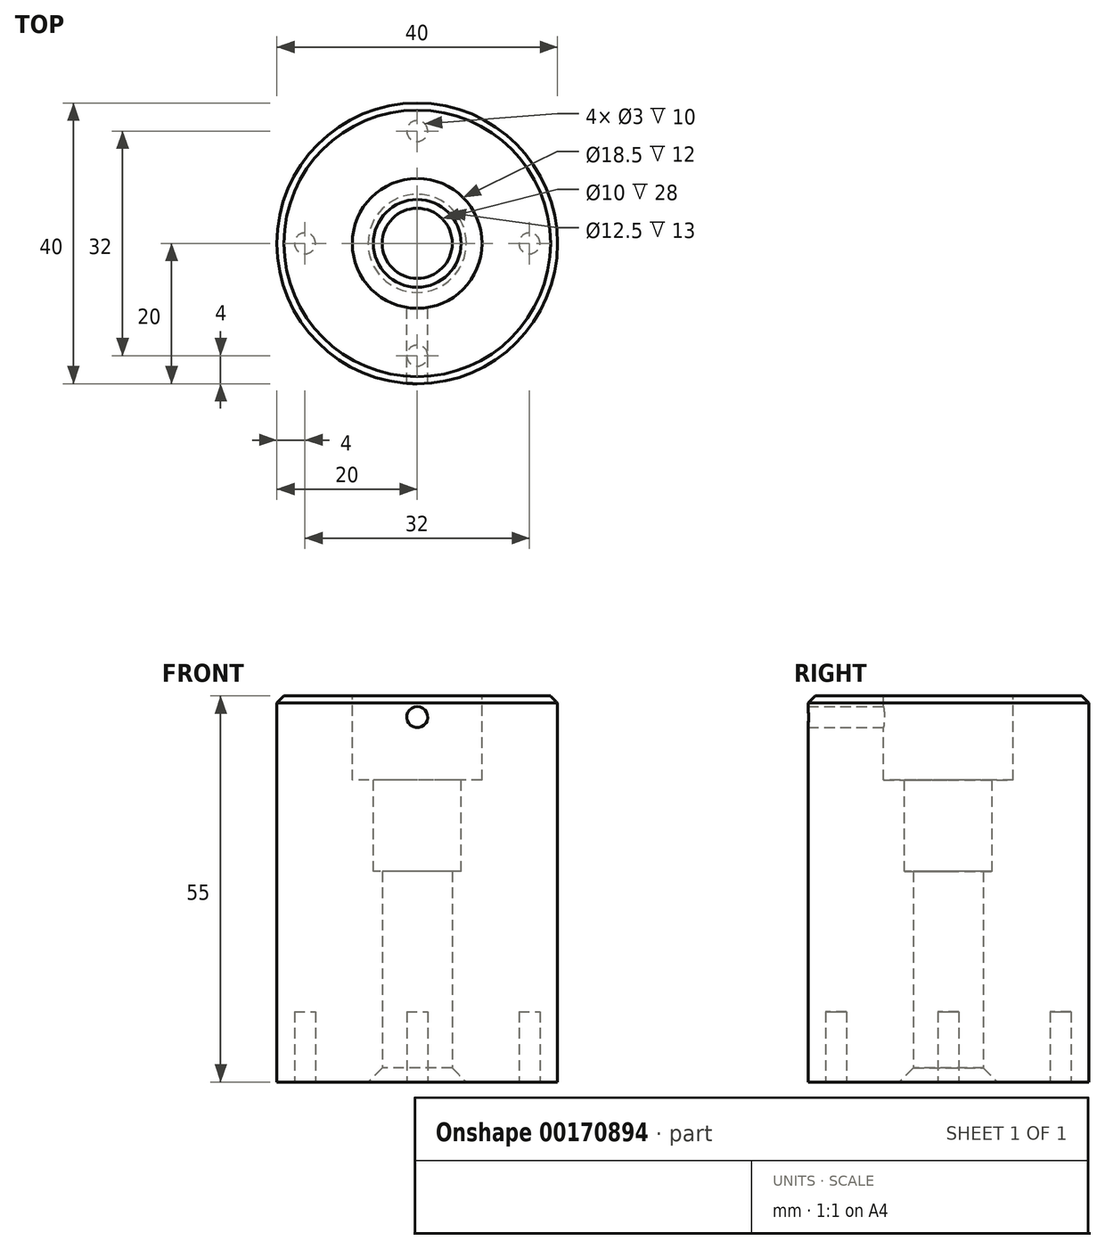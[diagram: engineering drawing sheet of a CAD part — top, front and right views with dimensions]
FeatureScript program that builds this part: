
annotation { "Feature Type Name" : "Feature", "Feature Type Description" : "" }
export const myFeature = defineFeature(function(context is Context, id is Id, definition is map)
    precondition{}
    {
        {
            var Q0;
            Q0=qCreatedBy(makeId("Top.planeOp"),FACE);
            var sketch = newSketch(context, id + "F0", { "sketchPlane" : qUnion([Q0])});
            skCircle(sketch, "E0", {"center": v(0, 0) * mm, "radius": 20 * mm});
            skCircle(sketch, "E1", {"center": v(0, 0) * mm, "radius": 5 * mm});
            skSolve(sketch);
        }
        {
            var Q0;
            Q0 = qSketchRegion(id + "F0", true);
            extrude(context, id + "F1", {"entities" : qUnion([Q0]), "depth" : 55 * mm});
        }
        {
            var Q0;
            Q0=makeQuery(id+"F1.opExtrude","CAP_FACE",FACE,{"disambiguationData":[OSD([sQuery(id+"F0.wireOp",EDGE,"E0"),sQuery(id+"F0.wireOp",EDGE,"E1")])],"isStart":false});
            var sketch = newSketch(context, id + "F2", { "sketchPlane" : qUnion([Q0])});
            skCircle(sketch, "E2", {"center": v(0, 0) * mm, "radius": 9.25 * mm});
            skSolve(sketch);
        }
        {
            var Q0;
            Q0 = qSketchRegion(id + "F2", true);
            extrude(context, id + "F3", {"entities" : qUnion([Q0]), "operationType" : NewBodyOperationType.REMOVE, "oppositeDirection" : true, "depth" : 12 * mm});
        }
        {
            var Q0;
            Q0=makeQuery(id+"F3.boolean.opBoolean","COPY",FACE,{"derivedFrom":makeQuery(id+"F3.opExtrude","CAP_FACE",FACE,{"disambiguationData":[OSD([sQuery(id+"F2.wireOp",EDGE,"E2")])],"isStart":false})});
            var sketch = newSketch(context, id + "F4", { "sketchPlane" : qUnion([Q0])});
            skCircle(sketch, "E3", {"center": v(0, 0) * mm, "radius": 6.25 * mm});
            skSolve(sketch);
        }
        {
            var Q0;
            Q0 = qSketchRegion(id + "F4", true);
            extrude(context, id + "F5", {"entities" : qUnion([Q0]), "operationType" : NewBodyOperationType.REMOVE, "oppositeDirection" : true, "depth" : 13 * mm});
        }
        {
            var Q0;
            Q0=makeQuery(id+"F3.boolean.opBoolean","COPY",EDGE,{"derivedFrom":makeQuery(id+"F3.opExtrude","CAP_EDGE",EDGE,{"disambiguationData":[OSD([sQuery(id+"F2.wireOp",EDGE,"E2")])],"isStart":true})});
            var Q1;
            Q1=makeQuery(id+"F1.opExtrude","CAP_EDGE",EDGE,{"disambiguationData":[OSD([sQuery(id+"F0.wireOp",EDGE,"E0")])],"isStart":false});
            chamfer(context, id + "F6", {"entities" : qUnion([Q0, Q1]), "width" : 1 * mm, "tangentPropagation" : true});
        }
        {
            var Q0;
            Q0=qCreatedBy(makeId("Front.planeOp"),FACE);
            var sketch = newSketch(context, id + "F7", { "sketchPlane" : qUnion([Q0])});
            skCircle(sketch, "E4", {"center": v(0, 52) * mm, "radius": 1.5 * mm});
            skSolve(sketch);
        }
        {
            var Q0;
            Q0 = qSketchRegion(id + "F7", true);
            extrude(context, id + "F8", {"entities" : qUnion([Q0]), "operationType" : NewBodyOperationType.REMOVE, "endBound" : BoundingType.THROUGH_ALL, "depth" : 25 * mm});
        }
        {
            var Q0;
            Q0=makeQuery(id+"F1.opExtrude","CAP_EDGE",EDGE,{"disambiguationData":[OSD([sQuery(id+"F0.wireOp",EDGE,"E1")])],"isStart":true});
            chamfer(context, id + "F9", {"entities" : qUnion([Q0]), "width" : 2 * mm, "tangentPropagation" : true});
        }
        {
            var Q0;
            Q0=makeQuery(id+"F1.opExtrude","CAP_FACE",FACE,{"disambiguationData":[OSD([sQuery(id+"F0.wireOp",EDGE,"E0"),sQuery(id+"F0.wireOp",EDGE,"E1")])],"isStart":true});
            var sketch = newSketch(context, id + "F10", { "sketchPlane" : qUnion([Q0])});
            skCircle(sketch, "E5", {"center": v(-16, 0) * mm, "radius": 1.5 * mm});
            skCircle(sketch, "E6", {"center": v(0, 16) * mm, "radius": 1.5 * mm});
            skCircle(sketch, "E7", {"center": v(16, 0) * mm, "radius": 1.5 * mm});
            skCircle(sketch, "E8", {"center": v(0, -16) * mm, "radius": 1.5 * mm});
            skSolve(sketch);
        }
        {
            var Q0;
            Q0 = qSketchRegion(id + "F10", true);
            extrude(context, id + "F11", {"entities" : qUnion([Q0]), "operationType" : NewBodyOperationType.REMOVE, "oppositeDirection" : true, "depth" : 10 * mm});
        }
    });
